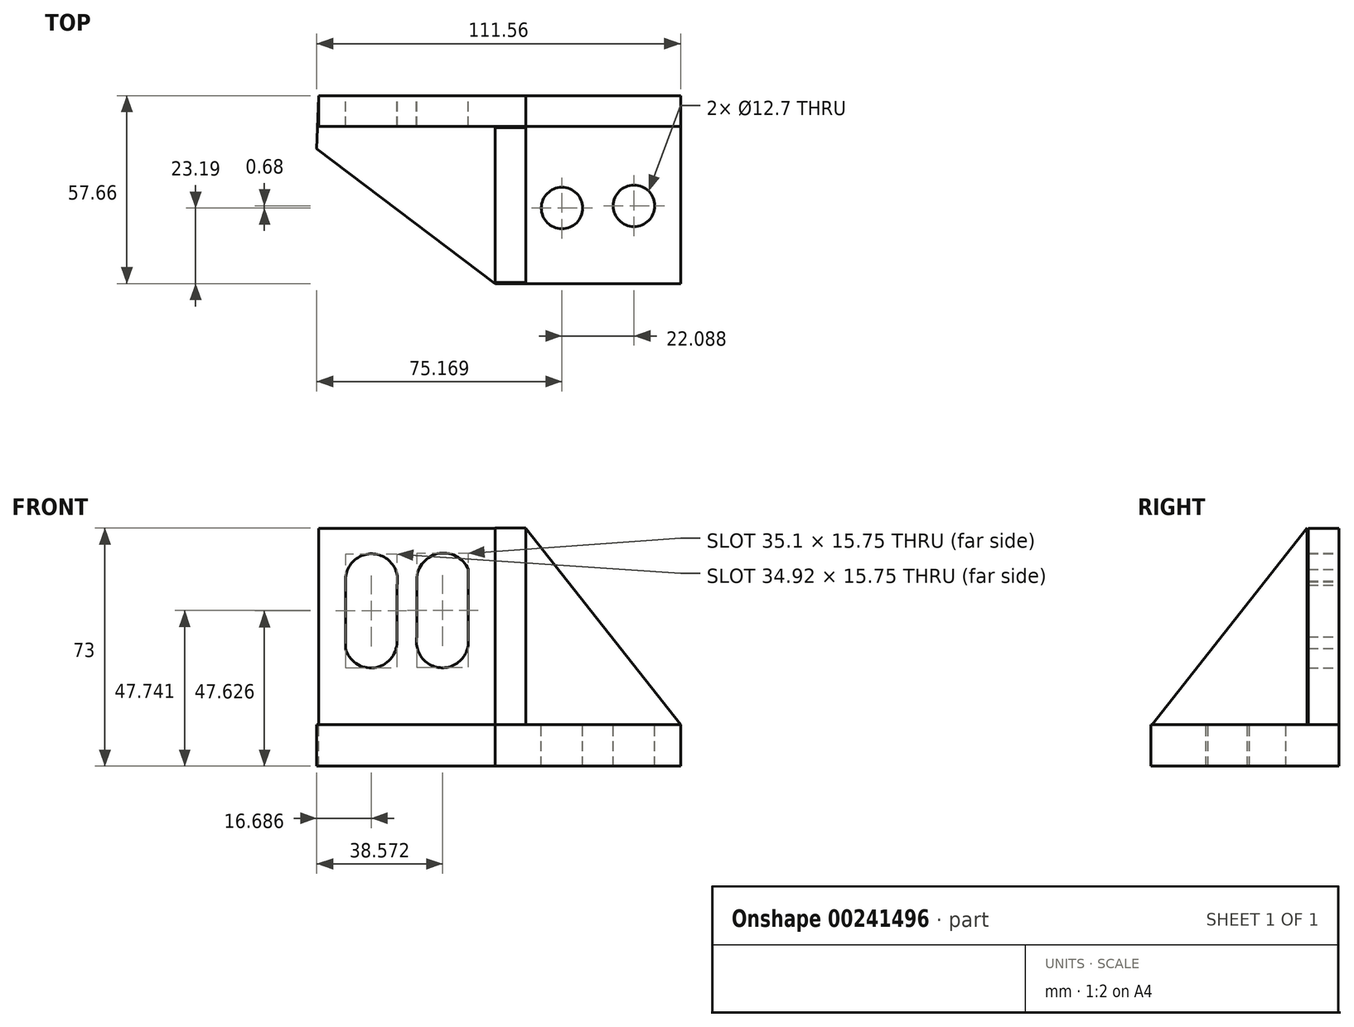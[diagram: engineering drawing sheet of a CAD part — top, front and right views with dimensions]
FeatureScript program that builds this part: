
annotation { "Feature Type Name" : "Feature", "Feature Type Description" : "" }
export const myFeature = defineFeature(function(context is Context, id is Id, definition is map)
    precondition{}
    {
        {
            var Q0;
            Q0=qCreatedBy(makeId("Front.planeOp"),FACE);
            var sketch = newSketch(context, id + "F0", { "sketchPlane" : qUnion([Q0])});
            skLineSegment(sketch, "E0", {"start": v(0, 60.2) * mm, "end": v(0, 0) * mm});
            skLineSegment(sketch, "E1", {"start": v(0, 0) * mm, "end": v(47.5, 0) * mm});
            skLineSegment(sketch, "E2", {"start": v(0, 60.2) * mm, "end": v(47.5, 0) * mm});
            skLineSegment(sketch, "E3", {"start": v(0, 60.2) * mm, "end": v(-63.5, 60.2) * mm});
            skLineSegment(sketch, "E4", {"start": v(-63.5, 60.2) * mm, "end": v(-63.5, 0) * mm});
            skLineSegment(sketch, "E5", {"start": v(-63.5, 0) * mm, "end": v(0, 0) * mm});
            skArc(sketch, "E6", {"start": v(-39.5, 42.76) * mm, "mid": v(-46.6, 52.39) * mm, "end": v(-55.24, 44.13) * mm});
            skArc(sketch, "E7", {"start": v(-17.6, 47.58) * mm, "mid": v(-27.1, 52.42) * mm, "end": v(-33.35, 43.78) * mm});
            skLineSegment(sketch, "E8", {"start": v(-55.24, 44.13) * mm, "end": v(-55.24, 23.44) * mm});
            skLineSegment(sketch, "E9", {"start": v(-39.5, 42.76) * mm, "end": v(-39.5, 25.4) * mm});
            skLineSegment(sketch, "E10", {"start": v(-33.35, 43.78) * mm, "end": v(-33.35, 26.93) * mm});
            skLineSegment(sketch, "E11", {"start": v(-17.6, 47.58) * mm, "end": v(-17.6, 25.4) * mm});
            skArc(sketch, "E12", {"start": v(-55.24, 23.44) * mm, "mid": v(-46.5, 17.47) * mm, "end": v(-39.5, 25.4) * mm});
            skArc(sketch, "E13", {"start": v(-33.35, 26.93) * mm, "mid": v(-26.32, 17.49) * mm, "end": v(-17.6, 25.4) * mm});
            skSolve(sketch);
        }
        {
            var Q0;
            Q0=makeQuery(id+"F0.imprint","IMPRINT",FACE,{"disambiguationData":[TD([[makeQuery(id+"F0.imprint","IMPRINT",EDGE,{"derivedFrom":sQuery(id+"F0.wireOp",EDGE,"E0")}),-1.0]])]});
            var Q1;
            Q1=makeQuery(id+"F0.imprint","IMPRINT",FACE,{"disambiguationData":[TD([[makeQuery(id+"F0.imprint","IMPRINT",EDGE,{"derivedFrom":sQuery(id+"F0.wireOp",EDGE,"E0")}),1.0]])]});
            extrude(context, id + "F1", {"entities" : qUnion([Q0, Q1]), "depth" : 9.4 * mm});
        }
        {
            var Q0;
            Q0=qCreatedBy(makeId("Top.planeOp"),FACE);
            var sketch = newSketch(context, id + "F2", { "sketchPlane" : qUnion([Q0])});
            skLineSegment(sketch, "E14", {"start": v(-63.48, 0) * mm, "end": v(47.51, 0) * mm});
            skLineSegment(sketch, "E15", {"start": v(47.51, 0) * mm, "end": v(47.51, -57.66) * mm});
            skLineSegment(sketch, "E16", {"start": v(47.51, -57.66) * mm, "end": v(-9.38, -57.66) * mm});
            skLineSegment(sketch, "E17", {"start": v(-9.38, -57.66) * mm, "end": v(-64.05, -16.25) * mm});
            skLineSegment(sketch, "E18", {"start": v(-64.05, -16.25) * mm, "end": v(-63.48, 0) * mm});
            skCircle(sketch, "E19", {"center": v(33.2, -33.8) * mm, "radius": 6.35 * mm});
            skCircle(sketch, "E20", {"center": v(11.12, -34.47) * mm, "radius": 6.35 * mm});
            skLineSegment(sketch, "E21", {"start": v(11.12, -34.47) * mm, "end": v(33.2, -33.8) * mm});
            skSolve(sketch);
        }
        {
            var Q0;
            Q0 = qSketchRegion(id + "F2", true);
            extrude(context, id + "F3", {"entities" : qUnion([Q0]), "operationType" : NewBodyOperationType.ADD, "oppositeDirection" : true, "depth" : 12.7 * mm});
        }
        {
            var Q0;
            Q0=qCreatedBy(makeId("Right.planeOp"),FACE);
            var sketch = newSketch(context, id + "F4", { "sketchPlane" : qUnion([Q0])});
            skLineSegment(sketch, "E22", {"start": v(-9.75, 60.3) * mm, "end": v(-9.75, 0) * mm});
            skLineSegment(sketch, "E23", {"start": v(-57.32, 0) * mm, "end": v(-9.75, 60.3) * mm});
            skLineSegment(sketch, "E24", {"start": v(-9.75, 0) * mm, "end": v(-57.32, 0) * mm});
            skSolve(sketch);
        }
        {
            var Q0;
            Q0=makeQuery(id+"F4.imprint","IMPRINT",FACE,{"disambiguationData":[TD([[makeQuery(id+"F4.imprint","IMPRINT",EDGE,{"derivedFrom":sQuery(id+"F4.wireOp",EDGE,"E22")}),-1.0]])]});
            extrude(context, id + "F5", {"entities" : qUnion([Q0]), "operationType" : NewBodyOperationType.ADD, "oppositeDirection" : true, "depth" : 9.4 * mm});
        }
    });
